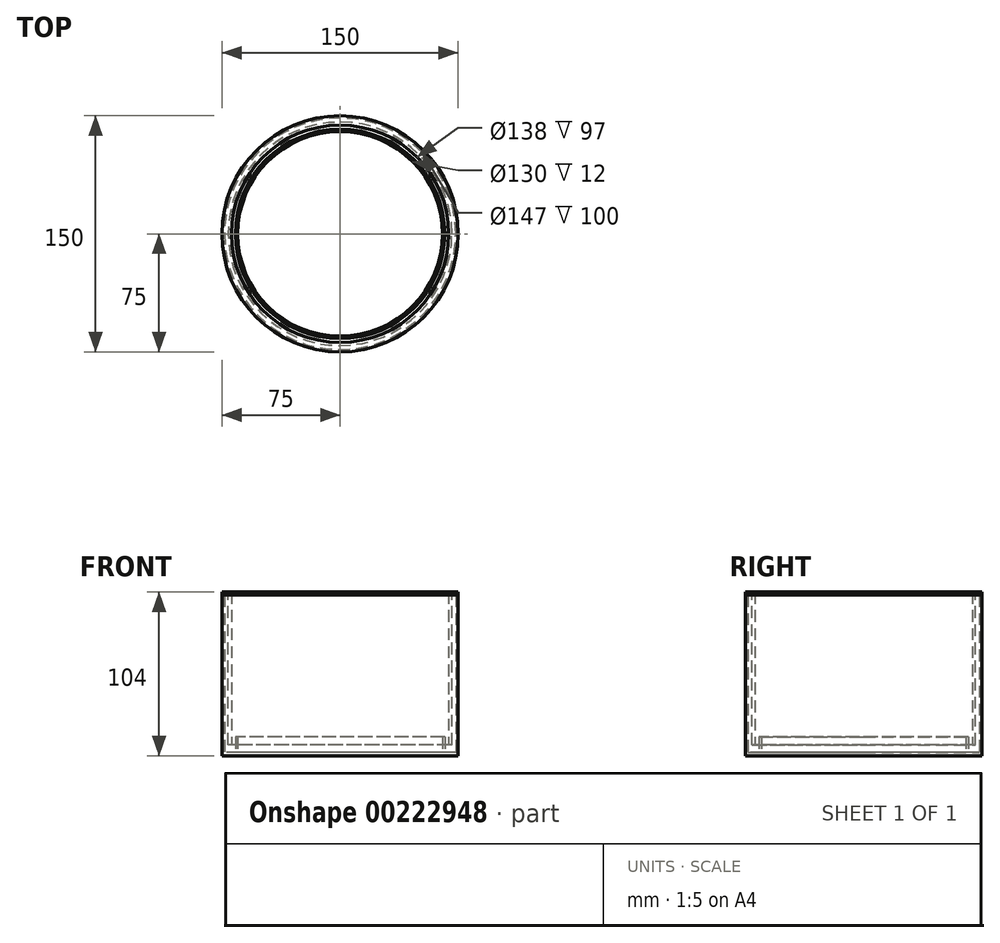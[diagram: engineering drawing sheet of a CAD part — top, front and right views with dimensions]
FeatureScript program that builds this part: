
annotation { "Feature Type Name" : "Feature", "Feature Type Description" : "" }
export const myFeature = defineFeature(function(context is Context, id is Id, definition is map)
    precondition{}
    {
        {
            var Q0;
            Q0=qCreatedBy(makeId("Top.planeOp"),FACE);
            var sketch = newSketch(context, id + "F0", { "sketchPlane" : qUnion([Q0])});
            skCircle(sketch, "E0", {"center": v(0, 0) * mm, "radius": 75 * mm});
            skCircle(sketch, "E1", {"center": v(0, 0) * mm, "radius": 65 * mm});
            skSolve(sketch);
        }
        {
            var Q0;
            Q0=makeQuery(id+"F0.imprint","IMPRINT",FACE,{"disambiguationData":[TD([[makeQuery(id+"F0.imprint","IMPRINT",EDGE,{"derivedFrom":sQuery(id+"F0.wireOp",EDGE,"E0")}),1.0]])]});
            extrude(context, id + "F1", {"entities" : qUnion([Q0]), "depth" : 2 * mm});
        }
        {
            var Q0;
            Q0=makeQuery(id+"F1.opExtrude","CAP_FACE",FACE,{"disambiguationData":[OSD([sQuery(id+"F0.wireOp",EDGE,"E0"),sQuery(id+"F0.wireOp",EDGE,"E1")])],"isStart":false});
            var sketch = newSketch(context, id + "F2", { "sketchPlane" : qUnion([Q0])});
            skCircle(sketch, "E2.0", {"center": v(0, 0) * mm, "radius": 73.5 * mm});
            skCircle(sketch, "E3.0", {"center": v(0, 0) * mm, "radius": 66.5 * mm});
            skSolve(sketch);
        }
        {
            var Q0;
            Q0=makeQuery(id+"F2.imprint","IMPRINT",FACE,{"disambiguationData":[TD([[makeQuery(id+"F2.imprint","IMPRINT",EDGE,{"derivedFrom":sQuery(id+"F2.wireOp",EDGE,"E3.0")}),1.0]])]});
            extrude(context, id + "F3", {"entities" : qUnion([Q0]), "operationType" : NewBodyOperationType.ADD, "depth" : 10 * mm});
        }
        {
            var Q0;
            Q0=makeQuery(id+"F2.imprint","IMPRINT",FACE,{"disambiguationData":[TD([[makeQuery(id+"F2.imprint","IMPRINT",EDGE,{"derivedFrom":sQuery(id+"F2.wireOp",EDGE,"E2.0")}),-1.0]])]});
            extrude(context, id + "F4", {"entities" : qUnion([Q0]), "operationType" : NewBodyOperationType.ADD, "depth" : 100 * mm});
        }
        {
            var Q0;
            Q0=makeQuery(id+"F4.opExtrude","CAP_FACE",FACE,{"disambiguationData":[OSD([sQuery(id+"F0.wireOp",EDGE,"E0"),sQuery(id+"F2.wireOp",EDGE,"E2.0")])],"isStart":false});
            var sketch = newSketch(context, id + "F5", { "sketchPlane" : qUnion([Q0])});
            skCircle(sketch, "E4", {"center": v(0, 0) * mm, "radius": 75 * mm});
            skCircle(sketch, "E5.0", {"center": v(0, 0) * mm, "radius": 69 * mm});
            skCircle(sketch, "E6", {"center": v(0, 0) * mm, "radius": 71 * mm});
            skSolve(sketch);
        }
        {
            var Q0;
            Q0 = qSketchRegion(id + "F5", true);
            var Q1;
            Q1=makeQuery(id+"F5.imprint","IMPRINT",FACE,{"disambiguationData":[TD([[makeQuery(id+"F5.imprint","IMPRINT",EDGE,{"derivedFrom":sQuery(id+"F5.wireOp",EDGE,"E5.0")}),-1.0]])]});
            extrude(context, id + "F6", {"entities" : qUnion([Q0, Q1]), "depth" : 2 * mm});
        }
        {
            var Q0;
            Q0=makeQuery(id+"F5.imprint","IMPRINT",FACE,{"disambiguationData":[TD([[makeQuery(id+"F5.imprint","IMPRINT",EDGE,{"derivedFrom":sQuery(id+"F5.wireOp",EDGE,"E5.0")}),-1.0]])]});
            extrude(context, id + "F7", {"entities" : qUnion([Q0]), "operationType" : NewBodyOperationType.ADD, "oppositeDirection" : true, "depth" : 95 * mm});
        }
        {
            var Q0;
            Q0=qCreatedBy(makeId("Front.planeOp"),FACE);
            cPlane(context, id + "F8", {"entities" : qUnion([Q0]), "cplaneType" : CPlaneType.OFFSET, "offset" : 75 * mm, "width" : 150 * mm, "height" : 150 * mm});
        }
    });
